# Revit family: Внешний водяной подогреватель 160-315
name_source: partatom
category: Оборудование
units: mm (PartAtom-declared; Revit-internal decimal feet)

## family parameters
Всегда вертикально = Нет
Классификация = Нет
На основе рабочей плоскости = Нет
Общий = Нет
При загрузке вырезать с полостями = Нет
Размер круглого соединителя = Использовать диаметр
Тип детали = Нормальный
Точка расчета площади = Нет

## types (4) — shared parameters
ADSK_Температура воздуха на выходе из нагревателя = 18 °C
C глубина = 200 мм
K1 x = 22 мм
ВВ высота = 50 мм
Коллектор D = 20 мм
СУ подкл = 19 мм
до оси трубы = 21 мм
опора d = 10 мм
zero-valued in all types: ADSK_Количество, ADSK_Масса

## per-type parameters (varying)
| type | 1 | A высота | ADSK_Расход воздуха приточный | ADSK_Расход теплоносителя | ADSK_Тепловая мощность | B ширина | Dn | Rn | z | Коллектор длина | Опора y1 | Опора y2 | Угол |
| WWK 250/2 | Смесительный узел ввп : WWK 250 | 276 мм | 620.0 м³/ч | 0.4 м³/ч | 9700 Вт | 345 мм | 250 мм | 125 мм | 50 мм | 206 мм | 78 мм | 100 мм | 21.80° |
| WWK 315/2 | Смесительный узел ввп : WWK 315 | 353 мм | 1000.0 м³/ч | 0.6 м³/ч | 16 Вт | 420 мм | 315 мм | 158 мм | 50 мм | 283 мм | 94 мм | 148 мм | 17.61° |
| WWK 160/2 | Смесительный узел ввп : WWK 160 | 203 мм | 260.0 м³/ч | 0.1 м³/ч | 4000 Вт | 270 мм | 160 мм | 80 мм | 30 мм | 283 мм | 49 мм | 86 мм | 32.01° |
| WWK 200/2 | Смесительный узел ввп : WWK 200 | 226 мм | 400.0 м³/ч | 0.2 м³/ч | 6200 Вт | 295 мм | 200 мм | 100 мм | 30 мм | 283 мм | 62 мм | 86 мм | 26.57° |

## geometry (parser evidence)
native form markers: Sweep x9
no freeform markers — native parametric forms only
